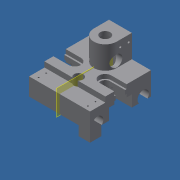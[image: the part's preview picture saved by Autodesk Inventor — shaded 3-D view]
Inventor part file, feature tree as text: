
AUTODESK INVENTOR PART (.ipt)
format: ipt  version: 2021 (Build 250183000, 183)  size: 477,696 bytes
history: native  units: mm
features: extrude x19, sketch x19, plane x3, mirror x2, other x1
ambient origin geometry x8: Origin, YZ Plane, XZ Plane, XY Plane, X Axis, Y Axis, Z Axis, Center Point
bodies: Solid1 (feature_tree)
feature tree (44):
  other  "<userpath>\OneDrive\Objet3D\3DPrinter\Parameters.xlsx"
  extrude  "Extrusion1"  Depth=80.0mm
  extrude  "Extrusion2"  Depth=40.0mm
  extrude  "Extrusion3"  Depth=20.0mm
  extrude  "Extrusion4"  Depth=10.0mm
  extrude  "Extrusion5"  Depth=5.5mm TaperAngle=0.0deg
  extrude  "Extrusion6"  Depth=4.0mm TaperAngle=0.0deg
  plane  "Work Plane1"
  mirror  "Mirror1"
  extrude  "Extrusion8"  Depth=8.1mm
  extrude  "Extrusion9"  Depth=25.0mm
  plane  "Work Plane2"
  mirror  "Mirror2"
  extrude  "Extrusion10"  Depth=15.0mm
  extrude  "Extrusion11"  Depth=5.0mm
  extrude  "Extrusion12"  Depth=5.0mm
  extrude  "Extrusion13"  Depth=80.0mm
  extrude  "Extrusion14"  Depth=15.0mm
  extrude  "Extrusion15"  Depth=10.0mm
  extrude  "Extrusion16"  Depth=10.0mm
  extrude  "Extrusion17"  TaperAngle=0.0deg  [1 undecoded]
  extrude  "Extrusion18"  Depth=1.9mm
  plane  "Work Plane3"
  extrude  "Extrusion19"  Depth=7.6mm
  extrude  "Extrusion20"  Depth=7.5mm
  sketch  "Sketch1"  dims[d0=80.0mm d1=80.0mm]
  sketch  "Sketch2"  dims[d2=15.0mm d3=0.0mm d7=40.0mm]
  sketch  "Sketch3"  dims[d8=20.0mm d9=12.2mm]
  sketch  "Sketch4"  dims[d10=10.0mm d11=0.0mm d12=16.2mm]
  sketch  "Sketch5"  dims[d13=4.0mm d14=0.0mm d15=5.5mm d16=0.0mm]
  sketch  "Sketch6"  dims[d17=13.8mm d18=4.0mm d19=0.0mm]
  sketch  "Sketch8"  dims[d20=16.2mm d21=8.1mm]
  sketch  "Sketch9"  dims[d22=25.0mm d23=25.0mm]
  sketch  "Sketch10"  dims[d24=15.0mm d25=15.0mm]
  sketch  "Sketch11"  dims[d29=15.0mm d30=5.0mm d31=5.0mm d32=15.0mm]
  sketch  "Sketch12"  dims[d33=5.0mm d34=5.0mm]
  sketch  "Sketch13"  dims[d35=80.0mm d36=0.0mm d37=0.0mm]
  sketch  "Sketch14"  dims[d38=15.0mm d39=15.0mm]
  sketch  "Sketch15"  dims[d40=60.0mm d41=10.0mm]
  sketch  "Sketch16"  dims[d42=10.0mm d49=20.2mm]
  sketch  "Sketch17"  dims[d50=7.0mm d51=0.0mm d52=0.0mm]
  sketch  "Sketch18"  dims[d53=1.9mm d54=1.9mm]
  sketch  "Sketch19"  dims[d55=7.6mm d56=7.6mm]
  sketch  "Sketch20"  dims[d57=10.0mm d58=4.9mm d59=10.0mm d60=0.0mm d61=12.0mm d62=20.0mm d63=0.0mm d64=30.0mm d65=20.0mm d66=40.0mm d67=20.0mm d68=30.0mm d69=0.0mm d70=13.0mm d71=5.0mm d72=0.0mm d73=35.0mm d74=0.0mm d75=2.9mm d76=2.9mm d77=11.0mm d78=4.0mm d79=8.5mm d80=8.5mm d81=15.0mm d82=0.0mm d83=6.0mm d84=15.0mm d85=8.0mm d86=17.0mm d87=0.0mm d88=15.0mm d89=0.0mm d90=32.5mm d91=15.0mm d92=15.0mm d93=32.5mm d94=45.0mm d95=0.0mm d96=7.5mm d97=7.5mm d98=15.0mm d99=32.5mm d100=0.0mm d101=-5.0mm d102=10.0mm d103=5.0mm d104=0.0mm d112=20.0mm d113=0.0mm d114=3.0mm d115=3.0mm d116=3.0mm d117=3.0mm d118=3.0mm d119=3.0mm d120=3.0mm d121=5.2mm d122=7.5mm]
note: 1 required parameter value undecoded (feature->parameter linkage not recoverable at this tier; creation-order binding heuristic only, values carry confidence <= 0.55)
